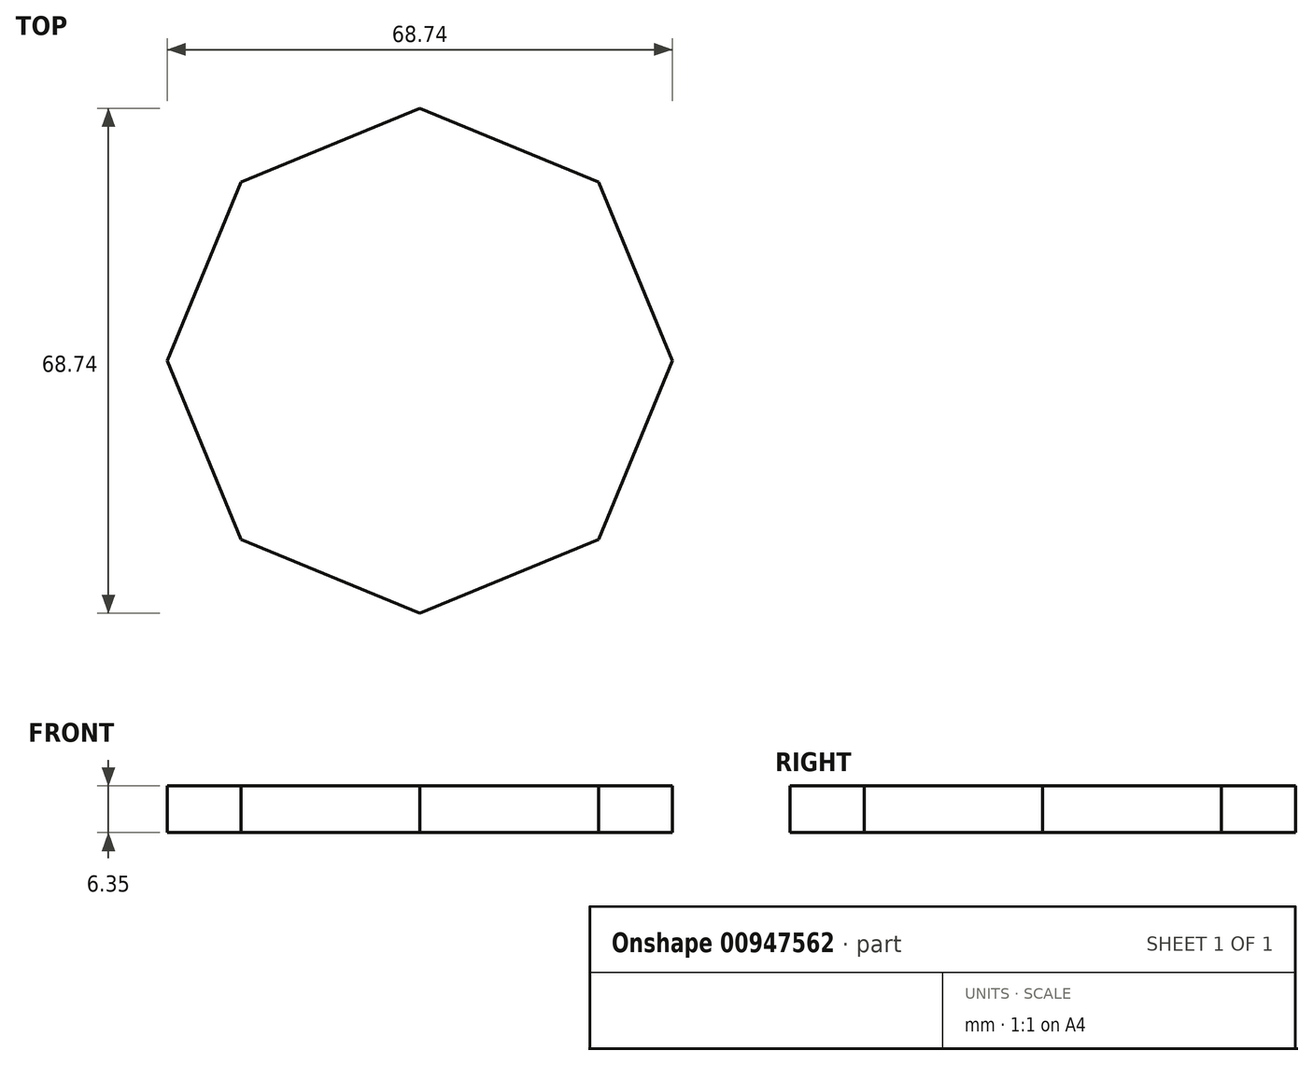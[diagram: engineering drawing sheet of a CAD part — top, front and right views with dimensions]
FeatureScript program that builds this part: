
annotation { "Feature Type Name" : "Feature", "Feature Type Description" : "" }
export const myFeature = defineFeature(function(context is Context, id is Id, definition is map)
    precondition{}
    {
        {
            var Q0;
            Q0=qCreatedBy(makeId("Top.planeOp"),FACE);
            var sketch = newSketch(context, id + "F0", { "sketchPlane" : qUnion([Q0])});
            skCircle(sketch, "E0.cCircle", {"center": v(0, 0) * mm, "radius": 31.75 * mm, "construction": true});
            skLineSegment(sketch, "E0.0", {"start": v(24.3, 24.3) * mm, "end": v(34.37, 0) * mm});
            skLineSegment(sketch, "E0.1", {"start": v(34.37, 0) * mm, "end": v(24.3, -24.3) * mm});
            skLineSegment(sketch, "E0.2", {"start": v(24.3, -24.3) * mm, "end": v(0, -34.37) * mm});
            skLineSegment(sketch, "E0.3", {"start": v(0, -34.37) * mm, "end": v(-24.3, -24.3) * mm});
            skLineSegment(sketch, "E0.4", {"start": v(-24.3, -24.3) * mm, "end": v(-34.37, 0) * mm});
            skLineSegment(sketch, "E0.5", {"start": v(-34.37, 0) * mm, "end": v(-24.3, 24.3) * mm});
            skLineSegment(sketch, "E0.6", {"start": v(-24.3, 24.3) * mm, "end": v(0, 34.37) * mm});
            skLineSegment(sketch, "E0.7", {"start": v(0, 34.37) * mm, "end": v(24.3, 24.3) * mm});
            skPoint(sketch, "E0.0.midPoint", {"position": v(29.33, 12.15) * mm});
            skLineSegment(sketch, "E1", {"start": v(0, 0) * mm, "end": v(-89.7, 0) * mm, "construction": true});
            skSolve(sketch);
        }
        {
            var Q0;
            Q0 = qSketchRegion(id + "F0", true);
            extrude(context, id + "F1", {"entities" : qUnion([Q0]), "depth" : 6.35 * mm, "offsetDistance" : 25.4 * mm});
        }
    });
